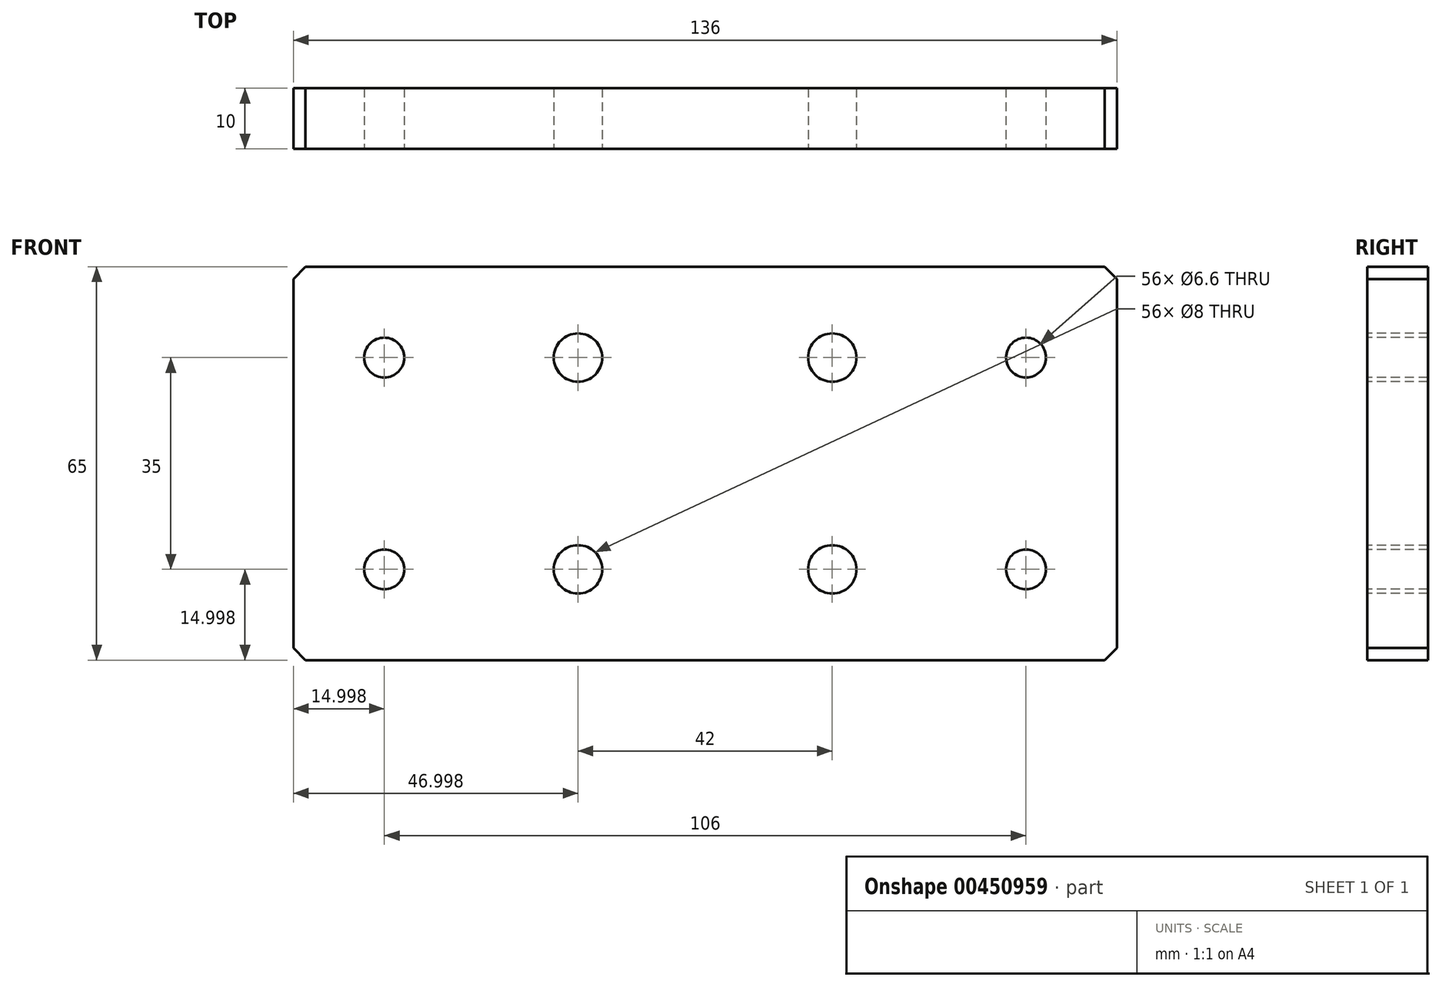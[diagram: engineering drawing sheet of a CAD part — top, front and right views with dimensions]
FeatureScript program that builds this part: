
annotation { "Feature Type Name" : "Feature", "Feature Type Description" : "" }
export const myFeature = defineFeature(function(context is Context, id is Id, definition is map)
    precondition{}
    {
        {
            var Q0;
            Q0=qCreatedBy(makeId("Front.planeOp"),FACE);
            var sketch = newSketch(context, id + "F0", { "sketchPlane" : qUnion([Q0])});
            skLineSegment(sketch, "E0", {"start": v(-109.43, -55.08) * mm, "end": v(22.57, -55.08) * mm});
            skLineSegment(sketch, "E1", {"start": v(74.43, -55.08) * mm, "end": v(74.43, -120.08) * mm});
            skLineSegment(sketch, "E2", {"start": v(83.43, -55.08) * mm, "end": v(83.43, -120.08) * mm});
            skLineSegment(sketch, "E3", {"start": v(-22.43, -111.08) * mm, "end": v(-22.43, -99.08) * mm});
            skCircle(sketch, "E4", {"center": v(-22.43, -105.08) * mm, "radius": 4 * mm});
            skLineSegment(sketch, "E5", {"start": v(-16.43, -105.08) * mm, "end": v(-28.43, -105.08) * mm});
            skCircle(sketch, "E6", {"center": v(-22.43, -105.08) * mm, "radius": 3.32 * mm});
            skLineSegment(sketch, "E7", {"start": v(83.43, -55.08) * mm, "end": v(74.43, -55.08) * mm});
            skLineSegment(sketch, "E8", {"start": v(83.43, -120.08) * mm, "end": v(74.43, -120.08) * mm});
            skLineSegment(sketch, "E9", {"start": v(-109.43, -120.08) * mm, "end": v(22.57, -120.08) * mm});
            skLineSegment(sketch, "E10", {"start": v(24.57, -118.08) * mm, "end": v(22.57, -120.08) * mm});
            skLineSegment(sketch, "E11", {"start": v(-109.43, -55.08) * mm, "end": v(-111.43, -57.08) * mm});
            skLineSegment(sketch, "E12", {"start": v(24.57, -57.08) * mm, "end": v(22.57, -55.08) * mm});
            skLineSegment(sketch, "E13", {"start": v(24.57, -57.08) * mm, "end": v(24.57, -118.08) * mm});
            skLineSegment(sketch, "E14", {"start": v(-111.43, -57.08) * mm, "end": v(-111.43, -118.08) * mm});
            skLineSegment(sketch, "E15", {"start": v(-109.43, -120.08) * mm, "end": v(-111.43, -118.08) * mm});
            skLineSegment(sketch, "E16", {"start": v(-22.43, -76.08) * mm, "end": v(-22.43, -64.08) * mm});
            skCircle(sketch, "E17", {"center": v(-22.43, -70.08) * mm, "radius": 4 * mm});
            skLineSegment(sketch, "E18", {"start": v(-16.43, -70.08) * mm, "end": v(-28.43, -70.08) * mm});
            skCircle(sketch, "E19", {"center": v(-22.43, -70.08) * mm, "radius": 3.32 * mm});
            skLineSegment(sketch, "E20", {"start": v(-64.43, -76.08) * mm, "end": v(-64.43, -64.08) * mm});
            skCircle(sketch, "E21", {"center": v(-64.43, -70.08) * mm, "radius": 4 * mm});
            skLineSegment(sketch, "E22", {"start": v(-58.43, -70.08) * mm, "end": v(-70.43, -70.08) * mm});
            skCircle(sketch, "E23", {"center": v(-64.43, -70.08) * mm, "radius": 3.32 * mm});
            skLineSegment(sketch, "E24", {"start": v(-64.43, -111.08) * mm, "end": v(-64.43, -99.08) * mm});
            skCircle(sketch, "E25", {"center": v(-64.43, -105.08) * mm, "radius": 4 * mm});
            skLineSegment(sketch, "E26", {"start": v(-58.43, -105.08) * mm, "end": v(-70.43, -105.08) * mm});
            skCircle(sketch, "E27", {"center": v(-64.43, -105.08) * mm, "radius": 3.32 * mm});
            skLineSegment(sketch, "E28", {"start": v(5.02, -70.08) * mm, "end": v(14.12, -70.08) * mm});
            skLineSegment(sketch, "E29", {"start": v(9.57, -74.63) * mm, "end": v(9.57, -65.53) * mm});
            skLineSegment(sketch, "E30", {"start": v(5.02, -105.08) * mm, "end": v(14.12, -105.08) * mm});
            skLineSegment(sketch, "E31", {"start": v(9.57, -109.63) * mm, "end": v(9.57, -100.53) * mm});
            skLineSegment(sketch, "E32", {"start": v(-100.98, -70.08) * mm, "end": v(-91.88, -70.08) * mm});
            skLineSegment(sketch, "E33", {"start": v(-96.43, -74.63) * mm, "end": v(-96.43, -65.53) * mm});
            skLineSegment(sketch, "E34", {"start": v(-100.98, -105.08) * mm, "end": v(-91.88, -105.08) * mm});
            skLineSegment(sketch, "E35", {"start": v(-96.43, -109.63) * mm, "end": v(-96.43, -100.53) * mm});
            skCircle(sketch, "E36", {"center": v(9.57, -105.08) * mm, "radius": 3.3 * mm});
            skCircle(sketch, "E37", {"center": v(9.57, -70.08) * mm, "radius": 3.3 * mm});
            skCircle(sketch, "E38", {"center": v(-96.43, -70.08) * mm, "radius": 3.3 * mm});
            skCircle(sketch, "E39", {"center": v(-96.43, -105.08) * mm, "radius": 3.3 * mm});
            skSolve(sketch);
        }
        {
            var Q0;
            Q0=makeQuery(id+"F0.imprint","IMPRINT",FACE,{"disambiguationData":[TD([[makeQuery(id+"F0.imprint","IMPRINT",EDGE,{"derivedFrom":sQuery(id+"F0.wireOp",EDGE,"E0")}),-1.0]])]});
            extrude(context, id + "F1", {"entities" : qUnion([Q0]), "oppositeDirection" : true, "depth" : 10 * mm});
        }
    });
